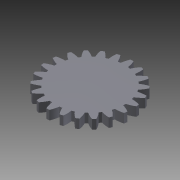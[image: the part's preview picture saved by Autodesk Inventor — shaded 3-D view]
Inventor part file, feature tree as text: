
AUTODESK INVENTOR PART (.ipt)
format: ipt  version: 2014 SP2 (Build 180246200, 246)  size: 246,272 bytes
history: native  units: mm (DEFAULTED — no unit token found)
features: plane x4, sketch x4, other x3, extrude x2, hole x2, projected_geometry x1
ambient origin geometry x8: Origin, YZ Plane, XZ Plane, XY Plane, X Axis, Y Axis, Z Axis, Center Point
bodies: Solid1 (feature_tree)
feature tree (16):
  extrude  "Extrusion1"  Depth=6.0mm TaperAngle=0.0deg
  plane  "Work Plane2"
  plane  "Work Plane8"
  plane  "Work Plane9"
  other  "Spur Gear"
  extrude  "Extrusion2"  Depth=10.0mm TaperAngle=0.0deg
  plane  "Work Plane11"
  hole  "Hole1"  [1 undecoded]
  hole  "Hole2"  [1 undecoded]
  sketch  "Sketch1"  dims[d0=55.359411mm d1=6.0mm d2=0.0mm]
  sketch  "Sketch2"  dims[d3=49.956015mm d4=10.0mm d5=0.0mm]
  other  "Srf1"
  sketch  "Sketch3"  dims[d16=71.527931mm d17=0.0mm d34=1.427997mm]
  sketch  "Sketch4"  dims[d39=0.0mm d41=0.0mm d43=71.527931mm d46=71.527931mm d47=0.0mm d48=0.0mm d49=11.0mm d50=8.0mm d51=0.0mm d52=4.0mm d53=3.3mm d54=6.0mm d55=4.0mm d56=2.0mm d57=90.0deg d58=8.0mm d59=20.594885mm d60=10.0mm d61=10.0mm d62=5.5mm d63=6.0mm d64=4.0mm d65=2.0mm d66=90.0deg d67=8.0mm d68=20.594885mm]
  projected_geometry  "Projected Loop1"
  other  "Pitch Diameter"
note: 2 required parameter values undecoded (feature->parameter linkage not recoverable at this tier; creation-order binding heuristic only, values carry confidence <= 0.55)
